# Revit family: QUBE
name_source: partatom
category: Generic Models
revit_build: Autodesk Revit LT 2018 (Build: 20170927_1515(x64)
units: mm (PartAtom-declared; Revit-internal decimal feet)

## family parameters
Always vertical = Yes
Can host rebar = No
Cut with Voids When Loaded = No
Part Type = Normal
Room Calculation Point = No
Round Connector Dimension = Use Diameter
Shared = No
Work Plane-Based = Yes

## types (4) — shared parameters
Default Elevation = 4' - 0"

## per-type parameters (varying)
| type | 2' | 4' | 6' | 8' | CEILING | FIXTURE HEIGHT | FIXTURE HOLE | FIXTURE LENGTH |
| 2' | Yes | No | No | No | 12' - 0" | 8' - 0" | 0' - 11 3/8" | 1' - 1 1/8" |
| 4' | No | Yes | No | No | 8' - 6 23/32" | 6' - 0" | 1' - 11 3/8" | 2' - 1 1/8" |
| 6' | No | No | Yes | No | 8' - 6 23/32" | 6' - 0" | 2' - 11 3/8" | 3' - 1 1/8" |
| 8' | No | No | No | Yes | 15' - 0" | 8' - 0" | 3' - 11 3/8" | 4' - 1 1/8" |

## geometry (parser evidence)
native form markers: Sweep x5
no freeform markers — native parametric forms only
